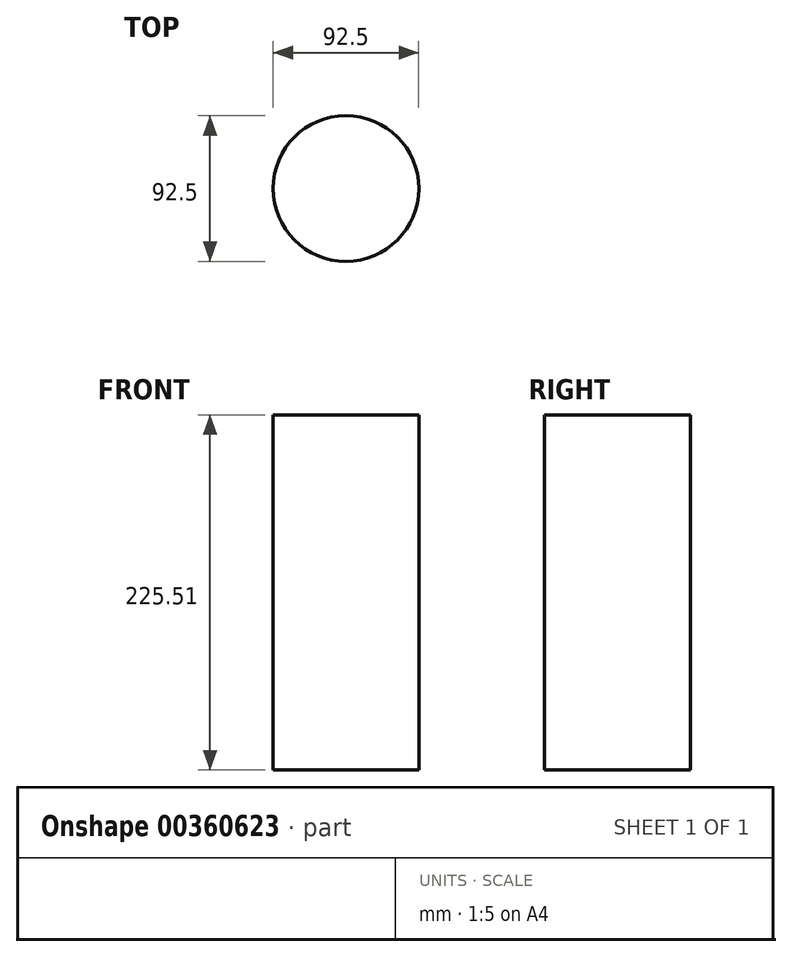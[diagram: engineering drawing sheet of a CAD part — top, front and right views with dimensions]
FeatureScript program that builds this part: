
annotation { "Feature Type Name" : "Feature", "Feature Type Description" : "" }
export const myFeature = defineFeature(function(context is Context, id is Id, definition is map)
    precondition{}
    {
        {
            var Q0;
            Q0=qCreatedBy(makeId("Top.planeOp"),FACE);
            var sketch = newSketch(context, id + "F0", { "sketchPlane" : qUnion([Q0])});
            skCircle(sketch, "E0", {"center": v(0, 0) * mm, "radius": 46.25 * mm});
            skSolve(sketch);
        }
        {
            var Q0;
            Q0=makeQuery(id+"F0.imprint","IMPRINT",FACE,{"disambiguationData":[TD([[makeQuery(id+"F0.imprint","IMPRINT",EDGE,{"derivedFrom":sQuery(id+"F0.wireOp",EDGE,"E0")}),1.0]])]});
            extrude(context, id + "F1", {"entities" : qUnion([Q0]), "depth" : 225.5 * mm});
        }
    });
